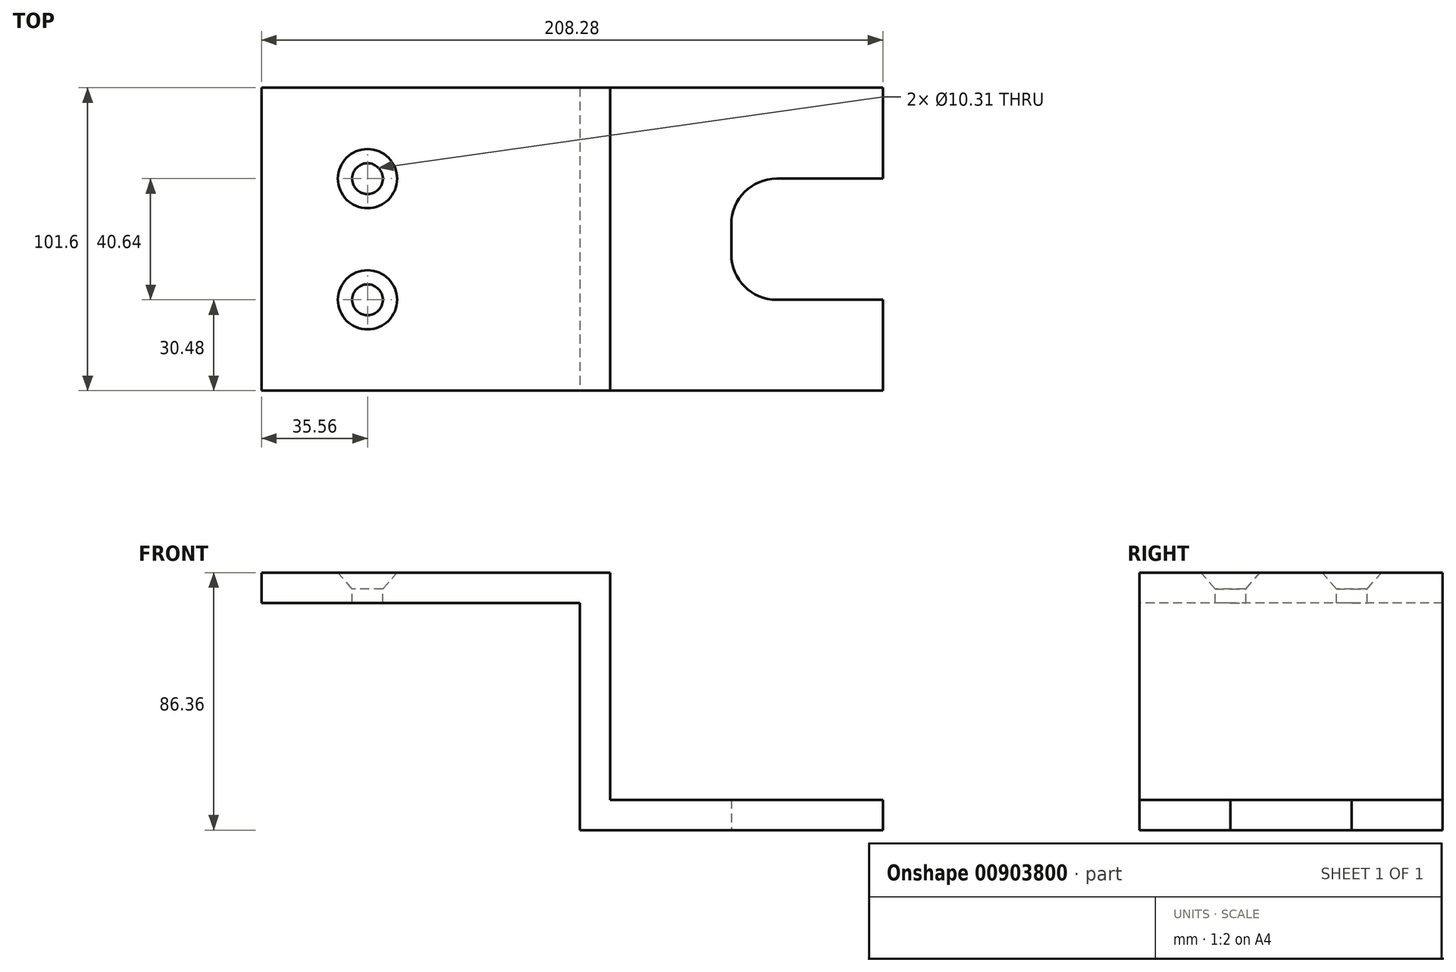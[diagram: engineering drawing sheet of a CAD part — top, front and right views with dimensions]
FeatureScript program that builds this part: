
annotation { "Feature Type Name" : "Feature", "Feature Type Description" : "" }
export const myFeature = defineFeature(function(context is Context, id is Id, definition is map)
    precondition{}
    {
        {
            var Q0;
            Q0=qCreatedBy(makeId("Front.planeOp"),FACE);
            var sketch = newSketch(context, id + "F0", { "sketchPlane" : qUnion([Q0])});
            skLineSegment(sketch, "E0.bottom", {"start": v(0, 10.16) * mm, "end": v(101.6, 10.16) * mm});
            skLineSegment(sketch, "E0.top", {"start": v(0, 0) * mm, "end": v(101.6, 0) * mm});
            skLineSegment(sketch, "E0.left", {"start": v(0, 10.16) * mm, "end": v(0, 0) * mm});
            skLineSegment(sketch, "E0.right", {"start": v(101.6, 10.16) * mm, "end": v(101.6, 0) * mm});
            skLineSegment(sketch, "E1.bottom", {"start": v(0, 86.36) * mm, "end": v(10.16, 86.36) * mm});
            skLineSegment(sketch, "E1.top", {"start": v(0, 10.16) * mm, "end": v(10.16, 10.16) * mm});
            skLineSegment(sketch, "E1.left", {"start": v(0, 86.36) * mm, "end": v(0, 10.16) * mm});
            skLineSegment(sketch, "E1.right", {"start": v(10.16, 86.36) * mm, "end": v(10.16, 10.16) * mm});
            skLineSegment(sketch, "E2.bottom", {"start": v(-106.68, 86.36) * mm, "end": v(0, 86.36) * mm});
            skLineSegment(sketch, "E2.top", {"start": v(-106.68, 76.2) * mm, "end": v(0, 76.2) * mm});
            skLineSegment(sketch, "E2.left", {"start": v(-106.68, 86.36) * mm, "end": v(-106.68, 76.2) * mm});
            skLineSegment(sketch, "E2.right", {"start": v(0, 86.36) * mm, "end": v(0, 76.2) * mm});
            skSolve(sketch);
        }
        {
            var Q0;
            Q0=qCreatedBy(makeId("Top.planeOp"),FACE);
            var sketch = newSketch(context, id + "F1", { "sketchPlane" : qUnion([Q0])});
            skLineSegment(sketch, "E3.bottom", {"start": v(-106.68, 50.8) * mm, "end": v(101.6, 50.8) * mm});
            skLineSegment(sketch, "E3.top", {"start": v(-106.68, -50.8) * mm, "end": v(101.6, -50.8) * mm});
            skLineSegment(sketch, "E3.left", {"start": v(-106.68, 50.8) * mm, "end": v(-106.68, -50.8) * mm});
            skLineSegment(sketch, "E3.right", {"start": v(101.6, 50.8) * mm, "end": v(101.6, -50.8) * mm});
            skLineSegment(sketch, "E4.bottom", {"start": v(50.8, 20.32) * mm, "end": v(101.6, 20.32) * mm});
            skLineSegment(sketch, "E4.top", {"start": v(50.8, -20.32) * mm, "end": v(101.6, -20.32) * mm});
            skLineSegment(sketch, "E4.left", {"start": v(50.8, 20.32) * mm, "end": v(50.8, -20.32) * mm});
            skLineSegment(sketch, "E4.right", {"start": v(101.6, 20.32) * mm, "end": v(101.6, -20.32) * mm});
            skPoint(sketch, "E5", {"position": v(-71.12, 20.32) * mm});
            skPoint(sketch, "E6", {"position": v(-71.12, -20.32) * mm});
            skSolve(sketch);
        }
        {
            var Q0;
            Q0 = qSketchRegion(id + "F0", true);
            var Q1;
            Q1=sQuery(id+"F1.wireOp",VERTEX,"E3.bottom.end");
            var Q2;
            Q2=sQuery(id+"F1.wireOp",VERTEX,"E3.top.end");
            extrude(context, id + "F2", {"entities" : qUnion([Q0]), "endBound" : BoundingType.UP_TO_VERTEX, "oppositeDirection" : true, "depth" : 25.4 * mm, "endBoundEntityVertex" : qUnion([Q1]), "offsetDistance" : 25.4 * mm, "hasSecondDirection" : true, "secondDirectionBound" : SecondDirectionBoundingType.UP_TO_VERTEX, "secondDirectionOppositeDirection" : false, "secondDirectionDepth" : 25.4 * mm, "secondDirectionBoundEntityVertex" : qUnion([Q2])});
        }
        {
            var Q0;
            Q0=makeQuery(id+"F2.opExtrude","SWEPT_FACE",FACE,{"disambiguationData":[OSD([sQuery(id+"F0.wireOp",EDGE,"E1.bottom"),sQuery(id+"F0.wireOp",EDGE,"E2.bottom")])]});
            var sketch = newSketch(context, id + "F3", { "sketchPlane" : qUnion([Q0])});
            skPoint(sketch, "E7", {"position": v(-71.12, 20.32) * mm});
            skPoint(sketch, "E8", {"position": v(-71.12, -20.32) * mm});
            skSolve(sketch);
        }
        {
            var Q0;
            Q0=makeQuery(id+"F1.imprint","IMPRINT",FACE,{"disambiguationData":[TD([[makeQuery(id+"F1.imprint","IMPRINT",EDGE,{"derivedFrom":sQuery(id+"F1.wireOp",EDGE,"E4.bottom")}),-1.0]])]});
            var Q1;
            Q1=makeQuery(id+"F2.opExtrude","SWEPT_FACE",FACE,{"disambiguationData":[OSD([sQuery(id+"F0.wireOp",EDGE,"E0.bottom")])]});
            extrude(context, id + "F4", {"entities" : qUnion([Q0]), "operationType" : NewBodyOperationType.REMOVE, "endBound" : BoundingType.UP_TO_SURFACE, "depth" : 25.4 * mm, "endBoundEntityFace" : qUnion([Q1]), "offsetDistance" : 25.4 * mm});
        }
        {
            var Q0;
            Q0=sQuery(id+"F3.wireOp",VERTEX,"E8");
            var Q1;
            Q1=sQuery(id+"F3.wireOp",VERTEX,"E7");
            var Q2;
            Q2=makeQuery(id+"F2.opExtrude","SWEPT_BODY",BODY,{"disambiguationData":[OSD([sQuery(id+"F0.wireOp",EDGE,"E0.bottom"),sQuery(id+"F0.wireOp",EDGE,"E0.top"),sQuery(id+"F0.wireOp",EDGE,"E0.left"),sQuery(id+"F0.wireOp",EDGE,"E0.right"),sQuery(id+"F0.wireOp",EDGE,"E1.bottom"),sQuery(id+"F0.wireOp",EDGE,"E1.left"),sQuery(id+"F0.wireOp",EDGE,"E1.right"),sQuery(id+"F0.wireOp",EDGE,"E2.bottom"),sQuery(id+"F0.wireOp",EDGE,"E2.top"),sQuery(id+"F0.wireOp",EDGE,"E2.left")])]});
            hole(context, id + "F5", {"style" : HoleStyle.C_SINK, "endStyle" : HoleEndStyle.THROUGH, "standardTappedOrClearance" : lookupTablePath({ "fit" : "Normal (ASME)", "standard" : "ANSI", "size" : "3/8", "type" : "Clearance" }), "standardBlindInLast" : lookupTablePath({ "fit" : "Normal", "standard" : "ANSI", "size" : "3/8", "type" : "Clearance" }), "holeDiameter" : 10.3 * mm, "cSinkDiameter" : 19.84 * mm, "cSinkAngle" : 82 * degree, "majorDiameter" : 6.35 * mm, "isTappedThrough" : true, "tappedDepth" : 12.7 * mm, "tapClearance" : 3, "startFromSketch" : true, "locations" : qUnion([Q0, Q1]), "scope" : qUnion([Q2])});
        }
        {
            var Q0;
            Q0=makeQuery(id+"F4.boolean.opBoolean","COPY",EDGE,{"derivedFrom":makeQuery(id+"F4.opExtrude","SWEPT_EDGE",EDGE,{"disambiguationData":[OSD([sQuery(id+"F1.wireOp",EDGE,"E4.bottom"),sQuery(id+"F1.wireOp",EDGE,"E4.left")])]})});
            var Q1;
            Q1=makeQuery(id+"F4.boolean.opBoolean","COPY",EDGE,{"derivedFrom":makeQuery(id+"F4.opExtrude","SWEPT_EDGE",EDGE,{"disambiguationData":[OSD([sQuery(id+"F1.wireOp",EDGE,"E4.top"),sQuery(id+"F1.wireOp",EDGE,"E4.left")])]})});
            fillet(context, id + "F6", {"entities" : qUnion([Q0, Q1]), "radius" : 15.24 * mm, "tangentPropagation" : true, "allowEdgeOverflow" : false});
        }
    });
